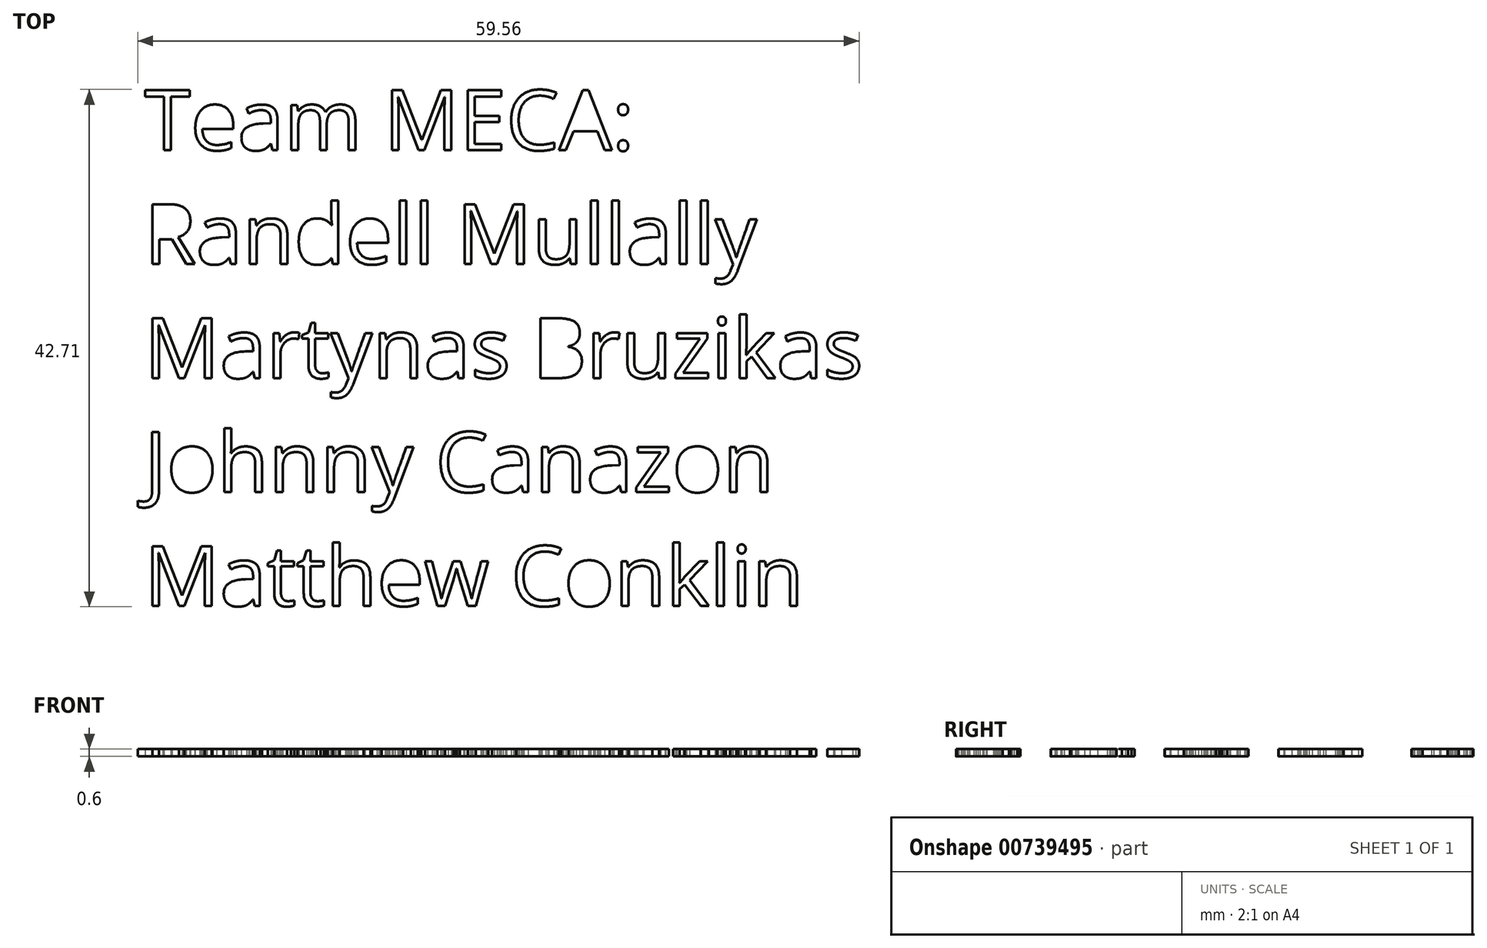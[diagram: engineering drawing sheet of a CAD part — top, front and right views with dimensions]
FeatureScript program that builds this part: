
annotation { "Feature Type Name" : "Feature", "Feature Type Description" : "" }
export const myFeature = defineFeature(function(context is Context, id is Id, definition is map)
    precondition{}
    {
        {
            var Q0;
            Q0=qCreatedBy(makeId("Top.planeOp"),FACE);
            var sketch = newSketch(context, id + "F0", { "sketchPlane" : qUnion([Q0])});
            skLineSegment(sketch, "E0.bottom", {"start": v(35, 50) * mm, "end": v(-35, 50) * mm});
            skLineSegment(sketch, "E0.top", {"start": v(35, -50) * mm, "end": v(-35, -50) * mm});
            skLineSegment(sketch, "E0.left", {"start": v(35, 50) * mm, "end": v(35, -50) * mm});
            skLineSegment(sketch, "E0.right", {"start": v(-35, 50) * mm, "end": v(-35, -50) * mm});
            skPoint(sketch, "E0.middle", {"position": v(0, 0) * mm});
            skText(sketch, "E1", { "text": "Team MECA:\nRandell Mullally\nMartynas Bruzikas\nJohnny Canazon\nMatthew Conklin", "fontName": "OpenSans-Regular.ttf"});
            const initialGuessF0  = {"E1": [-0.03, 0.03653, 1, 0, 0.00498]};
            skSetInitialGuess(sketch, initialGuessF0);
            skSolve(sketch);
        }
        {
            var Q0;
            Q0=makeQuery(id+"F0.imprint","IMPRINT",FACE,{"disambiguationData":[TD([[makeQuery(id+"F0.imprint","IMPRINT",EDGE,{"derivedFrom":sQuery(id+"F0.wireOp",EDGE,"E1.sketch_text.stroke-231")}),1.0]])]});
            var Q1;
            Q1=makeQuery(id+"F0.imprint","IMPRINT",FACE,{"disambiguationData":[TD([[makeQuery(id+"F0.imprint","IMPRINT",EDGE,{"derivedFrom":sQuery(id+"F0.wireOp",EDGE,"E1.sketch_text.stroke-254")}),1.0]])]});
            var Q2;
            Q2=makeQuery(id+"F0.imprint","IMPRINT",FACE,{"disambiguationData":[TD([[makeQuery(id+"F0.imprint","IMPRINT",EDGE,{"derivedFrom":sQuery(id+"F0.wireOp",EDGE,"E1.sketch_text.stroke-22")}),1.0]])]});
            var Q3;
            Q3=makeQuery(id+"F0.imprint","IMPRINT",FACE,{"disambiguationData":[TD([[makeQuery(id+"F0.imprint","IMPRINT",EDGE,{"derivedFrom":sQuery(id+"F0.wireOp",EDGE,"E1.sketch_text.stroke-46")}),1.0]])]});
            var Q4;
            Q4=makeQuery(id+"F0.imprint","IMPRINT",FACE,{"disambiguationData":[TD([[makeQuery(id+"F0.imprint","IMPRINT",EDGE,{"derivedFrom":sQuery(id+"F0.wireOp",EDGE,"E1.sketch_text.stroke-82")}),-1.0]])]});
            var Q5;
            Q5=makeQuery(id+"F0.imprint","IMPRINT",FACE,{"disambiguationData":[TD([[makeQuery(id+"F0.imprint","IMPRINT",EDGE,{"derivedFrom":sQuery(id+"F0.wireOp",EDGE,"E1.sketch_text.stroke-112")}),-1.0]])]});
            var Q6;
            Q6=makeQuery(id+"F0.imprint","IMPRINT",FACE,{"disambiguationData":[TD([[makeQuery(id+"F0.imprint","IMPRINT",EDGE,{"derivedFrom":sQuery(id+"F0.wireOp",EDGE,"E1.sketch_text.stroke-135")}),1.0]])]});
            var Q7;
            Q7=makeQuery(id+"F0.imprint","IMPRINT",FACE,{"disambiguationData":[TD([[makeQuery(id+"F0.imprint","IMPRINT",EDGE,{"derivedFrom":sQuery(id+"F0.wireOp",EDGE,"E1.sketch_text.stroke-165")}),1.0]])]});
            var Q8;
            Q8=makeQuery(id+"F0.imprint","IMPRINT",FACE,{"disambiguationData":[TD([[makeQuery(id+"F0.imprint","IMPRINT",EDGE,{"derivedFrom":sQuery(id+"F0.wireOp",EDGE,"E1.sketch_text.stroke-191")}),1.0]])]});
            var Q9;
            Q9=makeQuery(id+"F0.imprint","IMPRINT",FACE,{"disambiguationData":[TD([[makeQuery(id+"F0.imprint","IMPRINT",EDGE,{"derivedFrom":sQuery(id+"F0.wireOp",EDGE,"E1.sketch_text.stroke-1059")}),1.0]])]});
            var Q10;
            Q10=makeQuery(id+"F0.imprint","IMPRINT",FACE,{"disambiguationData":[TD([[makeQuery(id+"F0.imprint","IMPRINT",EDGE,{"derivedFrom":sQuery(id+"F0.wireOp",EDGE,"E1.sketch_text.stroke-746")}),-1.0]])]});
            var Q11;
            Q11=makeQuery(id+"F0.imprint","IMPRINT",FACE,{"disambiguationData":[TD([[makeQuery(id+"F0.imprint","IMPRINT",EDGE,{"derivedFrom":sQuery(id+"F0.wireOp",EDGE,"E1.sketch_text.stroke-615")}),-1.0]])]});
            var Q12;
            Q12=makeQuery(id+"F0.imprint","IMPRINT",FACE,{"disambiguationData":[TD([[makeQuery(id+"F0.imprint","IMPRINT",EDGE,{"derivedFrom":sQuery(id+"F0.wireOp",EDGE,"E1.sketch_text.stroke-534")}),1.0]])]});
            var Q13;
            Q13=makeQuery(id+"F0.imprint","IMPRINT",FACE,{"disambiguationData":[TD([[makeQuery(id+"F0.imprint","IMPRINT",EDGE,{"derivedFrom":sQuery(id+"F0.wireOp",EDGE,"E1.sketch_text.stroke-541")}),1.0]])]});
            var Q14;
            Q14=makeQuery(id+"F0.imprint","IMPRINT",FACE,{"disambiguationData":[TD([[makeQuery(id+"F0.imprint","IMPRINT",EDGE,{"derivedFrom":sQuery(id+"F0.wireOp",EDGE,"E1.sketch_text.stroke-329")}),1.0]])]});
            var Q15;
            Q15=makeQuery(id+"F0.imprint","IMPRINT",FACE,{"disambiguationData":[TD([[makeQuery(id+"F0.imprint","IMPRINT",EDGE,{"derivedFrom":sQuery(id+"F0.wireOp",EDGE,"E1.sketch_text.stroke-867")}),1.0]])]});
            var Q16;
            Q16=makeQuery(id+"F0.imprint","IMPRINT",FACE,{"disambiguationData":[TD([[makeQuery(id+"F0.imprint","IMPRINT",EDGE,{"derivedFrom":sQuery(id+"F0.wireOp",EDGE,"E1.sketch_text.stroke-8")}),-1.0]])]});
            var Q17;
            Q17=makeQuery(id+"F0.imprint","IMPRINT",FACE,{"disambiguationData":[TD([[makeQuery(id+"F0.imprint","IMPRINT",EDGE,{"derivedFrom":sQuery(id+"F0.wireOp",EDGE,"E1.sketch_text.stroke-398")}),1.0]])]});
            var Q18;
            Q18=makeQuery(id+"F0.imprint","IMPRINT",FACE,{"disambiguationData":[TD([[makeQuery(id+"F0.imprint","IMPRINT",EDGE,{"derivedFrom":sQuery(id+"F0.wireOp",EDGE,"E1.sketch_text.stroke-686")}),1.0]])]});
            var Q19;
            Q19=makeQuery(id+"F0.imprint","IMPRINT",FACE,{"disambiguationData":[TD([[makeQuery(id+"F0.imprint","IMPRINT",EDGE,{"derivedFrom":sQuery(id+"F0.wireOp",EDGE,"E1.sketch_text.stroke-0")}),-1.0]])]});
            var Q20;
            Q20=makeQuery(id+"F0.imprint","IMPRINT",FACE,{"disambiguationData":[TD([[makeQuery(id+"F0.imprint","IMPRINT",EDGE,{"derivedFrom":sQuery(id+"F0.wireOp",EDGE,"E1.sketch_text.stroke-54")}),-1.0]])]});
            var Q21;
            Q21=makeQuery(id+"F0.imprint","IMPRINT",FACE,{"disambiguationData":[TD([[makeQuery(id+"F0.imprint","IMPRINT",EDGE,{"derivedFrom":sQuery(id+"F0.wireOp",EDGE,"E1.sketch_text.stroke-100")}),-1.0]])]});
            var Q22;
            Q22=makeQuery(id+"F0.imprint","IMPRINT",FACE,{"disambiguationData":[TD([[makeQuery(id+"F0.imprint","IMPRINT",EDGE,{"derivedFrom":sQuery(id+"F0.wireOp",EDGE,"E1.sketch_text.stroke-140")}),-1.0]])]});
            var Q23;
            Q23=makeQuery(id+"F0.imprint","IMPRINT",FACE,{"disambiguationData":[TD([[makeQuery(id+"F0.imprint","IMPRINT",EDGE,{"derivedFrom":sQuery(id+"F0.wireOp",EDGE,"E1.sketch_text.stroke-148")}),-1.0]])]});
            var Q24;
            Q24=makeQuery(id+"F0.imprint","IMPRINT",FACE,{"disambiguationData":[TD([[makeQuery(id+"F0.imprint","IMPRINT",EDGE,{"derivedFrom":sQuery(id+"F0.wireOp",EDGE,"E1.sketch_text.stroke-199")}),-1.0]])]});
            var Q25;
            Q25=makeQuery(id+"F0.imprint","IMPRINT",FACE,{"disambiguationData":[TD([[makeQuery(id+"F0.imprint","IMPRINT",EDGE,{"derivedFrom":sQuery(id+"F0.wireOp",EDGE,"E1.sketch_text.stroke-490")}),1.0]])]});
            var Q26;
            Q26=makeQuery(id+"F0.imprint","IMPRINT",FACE,{"disambiguationData":[TD([[makeQuery(id+"F0.imprint","IMPRINT",EDGE,{"derivedFrom":sQuery(id+"F0.wireOp",EDGE,"E1.sketch_text.stroke-379")}),-1.0]])]});
            var Q27;
            Q27=makeQuery(id+"F0.imprint","IMPRINT",FACE,{"disambiguationData":[TD([[makeQuery(id+"F0.imprint","IMPRINT",EDGE,{"derivedFrom":sQuery(id+"F0.wireOp",EDGE,"E1.sketch_text.stroke-1035")}),-1.0]])]});
            var Q28;
            Q28=makeQuery(id+"F0.imprint","IMPRINT",FACE,{"disambiguationData":[TD([[makeQuery(id+"F0.imprint","IMPRINT",EDGE,{"derivedFrom":sQuery(id+"F0.wireOp",EDGE,"E1.sketch_text.stroke-729")}),-1.0]])]});
            var Q29;
            Q29=makeQuery(id+"F0.imprint","IMPRINT",FACE,{"disambiguationData":[TD([[makeQuery(id+"F0.imprint","IMPRINT",EDGE,{"derivedFrom":sQuery(id+"F0.wireOp",EDGE,"E1.sketch_text.stroke-240")}),-1.0]])]});
            var Q30;
            Q30=makeQuery(id+"F0.imprint","IMPRINT",FACE,{"disambiguationData":[TD([[makeQuery(id+"F0.imprint","IMPRINT",EDGE,{"derivedFrom":sQuery(id+"F0.wireOp",EDGE,"E1.sketch_text.stroke-1007")}),1.0]])]});
            var Q31;
            Q31=makeQuery(id+"F0.imprint","IMPRINT",FACE,{"disambiguationData":[TD([[makeQuery(id+"F0.imprint","IMPRINT",EDGE,{"derivedFrom":sQuery(id+"F0.wireOp",EDGE,"E1.sketch_text.stroke-694")}),-1.0]])]});
            var Q32;
            Q32=makeQuery(id+"F0.imprint","IMPRINT",FACE,{"disambiguationData":[TD([[makeQuery(id+"F0.imprint","IMPRINT",EDGE,{"derivedFrom":sQuery(id+"F0.wireOp",EDGE,"E1.sketch_text.stroke-438")}),-1.0]])]});
            var Q33;
            Q33=makeQuery(id+"F0.imprint","IMPRINT",FACE,{"disambiguationData":[TD([[makeQuery(id+"F0.imprint","IMPRINT",EDGE,{"derivedFrom":sQuery(id+"F0.wireOp",EDGE,"E1.sketch_text.stroke-310")}),-1.0]])]});
            var Q34;
            Q34=makeQuery(id+"F0.imprint","IMPRINT",FACE,{"disambiguationData":[TD([[makeQuery(id+"F0.imprint","IMPRINT",EDGE,{"derivedFrom":sQuery(id+"F0.wireOp",EDGE,"E1.sketch_text.stroke-1012")}),-1.0]])]});
            var Q35;
            Q35=makeQuery(id+"F0.imprint","IMPRINT",FACE,{"disambiguationData":[TD([[makeQuery(id+"F0.imprint","IMPRINT",EDGE,{"derivedFrom":sQuery(id+"F0.wireOp",EDGE,"E1.sketch_text.stroke-712")}),-1.0]])]});
            var Q36;
            Q36=makeQuery(id+"F0.imprint","IMPRINT",FACE,{"disambiguationData":[TD([[makeQuery(id+"F0.imprint","IMPRINT",EDGE,{"derivedFrom":sQuery(id+"F0.wireOp",EDGE,"E1.sketch_text.stroke-454")}),-1.0]])]});
            var Q37;
            Q37=makeQuery(id+"F0.imprint","IMPRINT",FACE,{"disambiguationData":[TD([[makeQuery(id+"F0.imprint","IMPRINT",EDGE,{"derivedFrom":sQuery(id+"F0.wireOp",EDGE,"E1.sketch_text.stroke-263")}),-1.0]])]});
            var Q38;
            Q38=makeQuery(id+"F0.imprint","IMPRINT",FACE,{"disambiguationData":[TD([[makeQuery(id+"F0.imprint","IMPRINT",EDGE,{"derivedFrom":sQuery(id+"F0.wireOp",EDGE,"E1.sketch_text.stroke-471")}),-1.0]])]});
            var Q39;
            Q39=makeQuery(id+"F0.imprint","IMPRINT",FACE,{"disambiguationData":[TD([[makeQuery(id+"F0.imprint","IMPRINT",EDGE,{"derivedFrom":sQuery(id+"F0.wireOp",EDGE,"E1.sketch_text.stroke-498")}),-1.0]])]});
            var Q40;
            Q40=makeQuery(id+"F0.imprint","IMPRINT",FACE,{"disambiguationData":[TD([[makeQuery(id+"F0.imprint","IMPRINT",EDGE,{"derivedFrom":sQuery(id+"F0.wireOp",EDGE,"E1.sketch_text.stroke-267")}),-1.0]])]});
            var Q41;
            Q41=makeQuery(id+"F0.imprint","IMPRINT",FACE,{"disambiguationData":[TD([[makeQuery(id+"F0.imprint","IMPRINT",EDGE,{"derivedFrom":sQuery(id+"F0.wireOp",EDGE,"E1.sketch_text.stroke-1067")}),-1.0]])]});
            var Q42;
            Q42=makeQuery(id+"F0.imprint","IMPRINT",FACE,{"disambiguationData":[TD([[makeQuery(id+"F0.imprint","IMPRINT",EDGE,{"derivedFrom":sQuery(id+"F0.wireOp",EDGE,"E1.sketch_text.stroke-762")}),-1.0]])]});
            var Q43;
            Q43=makeQuery(id+"F0.imprint","IMPRINT",FACE,{"disambiguationData":[TD([[makeQuery(id+"F0.imprint","IMPRINT",EDGE,{"derivedFrom":sQuery(id+"F0.wireOp",EDGE,"E1.sketch_text.stroke-285")}),-1.0]])]});
            var Q44;
            Q44=makeQuery(id+"F0.imprint","IMPRINT",FACE,{"disambiguationData":[TD([[makeQuery(id+"F0.imprint","IMPRINT",EDGE,{"derivedFrom":sQuery(id+"F0.wireOp",EDGE,"E1.sketch_text.stroke-677")}),-1.0]])]});
            var Q45;
            Q45=makeQuery(id+"F0.imprint","IMPRINT",FACE,{"disambiguationData":[TD([[makeQuery(id+"F0.imprint","IMPRINT",EDGE,{"derivedFrom":sQuery(id+"F0.wireOp",EDGE,"E1.sketch_text.stroke-1084")}),-1.0]])]});
            var Q46;
            Q46=makeQuery(id+"F0.imprint","IMPRINT",FACE,{"disambiguationData":[TD([[makeQuery(id+"F0.imprint","IMPRINT",EDGE,{"derivedFrom":sQuery(id+"F0.wireOp",EDGE,"E1.sketch_text.stroke-796")}),1.0]])]});
            var Q47;
            Q47=makeQuery(id+"F0.imprint","IMPRINT",FACE,{"disambiguationData":[TD([[makeQuery(id+"F0.imprint","IMPRINT",EDGE,{"derivedFrom":sQuery(id+"F0.wireOp",EDGE,"E1.sketch_text.stroke-302")}),-1.0]])]});
            var Q48;
            Q48=makeQuery(id+"F0.imprint","IMPRINT",FACE,{"disambiguationData":[TD([[makeQuery(id+"F0.imprint","IMPRINT",EDGE,{"derivedFrom":sQuery(id+"F0.wireOp",EDGE,"E1.sketch_text.stroke-777")}),-1.0]])]});
            var Q49;
            Q49=makeQuery(id+"F0.imprint","IMPRINT",FACE,{"disambiguationData":[TD([[makeQuery(id+"F0.imprint","IMPRINT",EDGE,{"derivedFrom":sQuery(id+"F0.wireOp",EDGE,"E1.sketch_text.stroke-1099")}),-1.0]])]});
            var Q50;
            Q50=makeQuery(id+"F0.imprint","IMPRINT",FACE,{"disambiguationData":[TD([[makeQuery(id+"F0.imprint","IMPRINT",EDGE,{"derivedFrom":sQuery(id+"F0.wireOp",EDGE,"E1.sketch_text.stroke-804")}),-1.0]])]});
            var Q51;
            Q51=makeQuery(id+"F0.imprint","IMPRINT",FACE,{"disambiguationData":[TD([[makeQuery(id+"F0.imprint","IMPRINT",EDGE,{"derivedFrom":sQuery(id+"F0.wireOp",EDGE,"E1.sketch_text.stroke-548")}),-1.0]])]});
            var Q52;
            Q52=makeQuery(id+"F0.imprint","IMPRINT",FACE,{"disambiguationData":[TD([[makeQuery(id+"F0.imprint","IMPRINT",EDGE,{"derivedFrom":sQuery(id+"F0.wireOp",EDGE,"E1.sketch_text.stroke-306")}),-1.0]])]});
            var Q53;
            Q53=makeQuery(id+"F0.imprint","IMPRINT",FACE,{"disambiguationData":[TD([[makeQuery(id+"F0.imprint","IMPRINT",EDGE,{"derivedFrom":sQuery(id+"F0.wireOp",EDGE,"E1.sketch_text.stroke-821")}),-1.0]])]});
            var Q54;
            Q54=makeQuery(id+"F0.imprint","IMPRINT",FACE,{"disambiguationData":[TD([[makeQuery(id+"F0.imprint","IMPRINT",EDGE,{"derivedFrom":sQuery(id+"F0.wireOp",EDGE,"E1.sketch_text.stroke-1103")}),-1.0]])]});
            var Q55;
            Q55=makeQuery(id+"F0.imprint","IMPRINT",FACE,{"disambiguationData":[TD([[makeQuery(id+"F0.imprint","IMPRINT",EDGE,{"derivedFrom":sQuery(id+"F0.wireOp",EDGE,"E1.sketch_text.stroke-840")}),1.0]])]});
            var Q56;
            Q56=makeQuery(id+"F0.imprint","IMPRINT",FACE,{"disambiguationData":[TD([[makeQuery(id+"F0.imprint","IMPRINT",EDGE,{"derivedFrom":sQuery(id+"F0.wireOp",EDGE,"E1.sketch_text.stroke-561")}),-1.0]])]});
            var Q57;
            Q57=makeQuery(id+"F0.imprint","IMPRINT",FACE,{"disambiguationData":[TD([[makeQuery(id+"F0.imprint","IMPRINT",EDGE,{"derivedFrom":sQuery(id+"F0.wireOp",EDGE,"E1.sketch_text.stroke-858")}),-1.0]])]});
            var Q58;
            Q58=makeQuery(id+"F0.imprint","IMPRINT",FACE,{"disambiguationData":[TD([[makeQuery(id+"F0.imprint","IMPRINT",EDGE,{"derivedFrom":sQuery(id+"F0.wireOp",EDGE,"E1.sketch_text.stroke-848")}),-1.0]])]});
            var Q59;
            Q59=makeQuery(id+"F0.imprint","IMPRINT",FACE,{"disambiguationData":[TD([[makeQuery(id+"F0.imprint","IMPRINT",EDGE,{"derivedFrom":sQuery(id+"F0.wireOp",EDGE,"E1.sketch_text.stroke-578")}),-1.0]])]});
            var Q60;
            Q60=makeQuery(id+"F0.imprint","IMPRINT",FACE,{"disambiguationData":[TD([[makeQuery(id+"F0.imprint","IMPRINT",EDGE,{"derivedFrom":sQuery(id+"F0.wireOp",EDGE,"E1.sketch_text.stroke-910")}),-1.0]])]});
            var Q61;
            Q61=makeQuery(id+"F0.imprint","IMPRINT",FACE,{"disambiguationData":[TD([[makeQuery(id+"F0.imprint","IMPRINT",EDGE,{"derivedFrom":sQuery(id+"F0.wireOp",EDGE,"E1.sketch_text.stroke-1115")}),-1.0]])]});
            var Q62;
            Q62=makeQuery(id+"F0.imprint","IMPRINT",FACE,{"disambiguationData":[TD([[makeQuery(id+"F0.imprint","IMPRINT",EDGE,{"derivedFrom":sQuery(id+"F0.wireOp",EDGE,"E1.sketch_text.stroke-588")}),-1.0]])]});
            var Q63;
            Q63=makeQuery(id+"F0.imprint","IMPRINT",FACE,{"disambiguationData":[TD([[makeQuery(id+"F0.imprint","IMPRINT",EDGE,{"derivedFrom":sQuery(id+"F0.wireOp",EDGE,"E1.sketch_text.stroke-875")}),-1.0]])]});
            var Q64;
            Q64=makeQuery(id+"F0.imprint","IMPRINT",FACE,{"disambiguationData":[TD([[makeQuery(id+"F0.imprint","IMPRINT",EDGE,{"derivedFrom":sQuery(id+"F0.wireOp",EDGE,"E1.sketch_text.stroke-341")}),-1.0]])]});
            var Q65;
            Q65=makeQuery(id+"F0.imprint","IMPRINT",FACE,{"disambiguationData":[TD([[makeQuery(id+"F0.imprint","IMPRINT",EDGE,{"derivedFrom":sQuery(id+"F0.wireOp",EDGE,"E1.sketch_text.stroke-993")}),-1.0]])]});
            var Q66;
            Q66=makeQuery(id+"F0.imprint","IMPRINT",FACE,{"disambiguationData":[TD([[makeQuery(id+"F0.imprint","IMPRINT",EDGE,{"derivedFrom":sQuery(id+"F0.wireOp",EDGE,"E1.sketch_text.stroke-892")}),-1.0]])]});
            var Q67;
            Q67=makeQuery(id+"F0.imprint","IMPRINT",FACE,{"disambiguationData":[TD([[makeQuery(id+"F0.imprint","IMPRINT",EDGE,{"derivedFrom":sQuery(id+"F0.wireOp",EDGE,"E1.sketch_text.stroke-600")}),-1.0]])]});
            var Q68;
            Q68=makeQuery(id+"F0.imprint","IMPRINT",FACE,{"disambiguationData":[TD([[makeQuery(id+"F0.imprint","IMPRINT",EDGE,{"derivedFrom":sQuery(id+"F0.wireOp",EDGE,"E1.sketch_text.stroke-345")}),-1.0]])]});
            var Q69;
            Q69=makeQuery(id+"F0.imprint","IMPRINT",FACE,{"disambiguationData":[TD([[makeQuery(id+"F0.imprint","IMPRINT",EDGE,{"derivedFrom":sQuery(id+"F0.wireOp",EDGE,"E1.sketch_text.stroke-1050")}),-1.0]])]});
            var Q70;
            Q70=makeQuery(id+"F0.imprint","IMPRINT",FACE,{"disambiguationData":[TD([[makeQuery(id+"F0.imprint","IMPRINT",EDGE,{"derivedFrom":sQuery(id+"F0.wireOp",EDGE,"E1.sketch_text.stroke-27")}),-1.0]])]});
            var Q71;
            Q71=makeQuery(id+"F0.imprint","IMPRINT",FACE,{"disambiguationData":[TD([[makeQuery(id+"F0.imprint","IMPRINT",EDGE,{"derivedFrom":sQuery(id+"F0.wireOp",EDGE,"E1.sketch_text.stroke-634")}),1.0]])]});
            var Q72;
            Q72=makeQuery(id+"F0.imprint","IMPRINT",FACE,{"disambiguationData":[TD([[makeQuery(id+"F0.imprint","IMPRINT",EDGE,{"derivedFrom":sQuery(id+"F0.wireOp",EDGE,"E1.sketch_text.stroke-361")}),-1.0]])]});
            var Q73;
            Q73=makeQuery(id+"F0.imprint","IMPRINT",FACE,{"disambiguationData":[TD([[makeQuery(id+"F0.imprint","IMPRINT",EDGE,{"derivedFrom":sQuery(id+"F0.wireOp",EDGE,"E1.sketch_text.stroke-523")}),-1.0]])]});
            var Q74;
            Q74=makeQuery(id+"F0.imprint","IMPRINT",FACE,{"disambiguationData":[TD([[makeQuery(id+"F0.imprint","IMPRINT",EDGE,{"derivedFrom":sQuery(id+"F0.wireOp",EDGE,"E1.sketch_text.stroke-127")}),-1.0]])]});
            var Q75;
            Q75=makeQuery(id+"F0.imprint","IMPRINT",FACE,{"disambiguationData":[TD([[makeQuery(id+"F0.imprint","IMPRINT",EDGE,{"derivedFrom":sQuery(id+"F0.wireOp",EDGE,"E1.sketch_text.stroke-937")}),-1.0]])]});
            var Q76;
            Q76=makeQuery(id+"F0.imprint","IMPRINT",FACE,{"disambiguationData":[TD([[makeQuery(id+"F0.imprint","IMPRINT",EDGE,{"derivedFrom":sQuery(id+"F0.wireOp",EDGE,"E1.sketch_text.stroke-642")}),-1.0]])]});
            var Q77;
            Q77=makeQuery(id+"F0.imprint","IMPRINT",FACE,{"disambiguationData":[TD([[makeQuery(id+"F0.imprint","IMPRINT",EDGE,{"derivedFrom":sQuery(id+"F0.wireOp",EDGE,"E1.sketch_text.stroke-154")}),-1.0]])]});
            var Q78;
            Q78=makeQuery(id+"F0.imprint","IMPRINT",FACE,{"disambiguationData":[TD([[makeQuery(id+"F0.imprint","IMPRINT",EDGE,{"derivedFrom":sQuery(id+"F0.wireOp",EDGE,"E1.sketch_text.stroke-956")}),-1.0]])]});
            var Q79;
            Q79=makeQuery(id+"F0.imprint","IMPRINT",FACE,{"disambiguationData":[TD([[makeQuery(id+"F0.imprint","IMPRINT",EDGE,{"derivedFrom":sQuery(id+"F0.wireOp",EDGE,"E1.sketch_text.stroke-667")}),-1.0]])]});
            var Q80;
            Q80=makeQuery(id+"F0.imprint","IMPRINT",FACE,{"disambiguationData":[TD([[makeQuery(id+"F0.imprint","IMPRINT",EDGE,{"derivedFrom":sQuery(id+"F0.wireOp",EDGE,"E1.sketch_text.stroke-406")}),-1.0]])]});
            var Q81;
            Q81=makeQuery(id+"F0.imprint","IMPRINT",FACE,{"disambiguationData":[TD([[makeQuery(id+"F0.imprint","IMPRINT",EDGE,{"derivedFrom":sQuery(id+"F0.wireOp",EDGE,"E1.sketch_text.stroke-172")}),-1.0]])]});
            var Q82;
            Q82=makeQuery(id+"F0.imprint","IMPRINT",FACE,{"disambiguationData":[TD([[makeQuery(id+"F0.imprint","IMPRINT",EDGE,{"derivedFrom":sQuery(id+"F0.wireOp",EDGE,"E1.sketch_text.stroke-975")}),-1.0]])]});
            var Q83;
            Q83=makeQuery(id+"F0.imprint","IMPRINT",FACE,{"disambiguationData":[TD([[makeQuery(id+"F0.imprint","IMPRINT",EDGE,{"derivedFrom":sQuery(id+"F0.wireOp",EDGE,"E1.sketch_text.stroke-419")}),-1.0]])]});
            var Q84;
            Q84=makeQuery(id+"F0.imprint","IMPRINT",FACE,{"disambiguationData":[TD([[makeQuery(id+"F0.imprint","IMPRINT",EDGE,{"derivedFrom":sQuery(id+"F0.wireOp",EDGE,"E1.sketch_text.stroke-216")}),-1.0]])]});
            var Q85;
            Q85=makeQuery(id+"F0.imprint","IMPRINT",FACE,{"disambiguationData":[TD([[makeQuery(id+"F0.imprint","IMPRINT",EDGE,{"derivedFrom":sQuery(id+"F0.wireOp",EDGE,"E1.sketch_text.stroke-259")}),-1.0]])]});
            var Q86;
            Q86=makeQuery(id+"F0.imprint","IMPRINT",FACE,{"disambiguationData":[TD([[makeQuery(id+"F0.imprint","IMPRINT",EDGE,{"derivedFrom":sQuery(id+"F0.wireOp",EDGE,"E1.sketch_text.stroke-1107")}),-1.0]])]});
            var Q87;
            Q87=makeQuery(id+"F0.imprint","IMPRINT",FACE,{"disambiguationData":[TD([[makeQuery(id+"F0.imprint","IMPRINT",EDGE,{"derivedFrom":sQuery(id+"F0.wireOp",EDGE,"E1.sketch_text.stroke-337")}),-1.0]])]});
            var Q88;
            Q88=makeQuery(id+"F0.imprint","IMPRINT",FACE,{"disambiguationData":[TD([[makeQuery(id+"F0.imprint","IMPRINT",EDGE,{"derivedFrom":sQuery(id+"F0.wireOp",EDGE,"E1.sketch_text.stroke-592")}),-1.0]])]});
            var Q89;
            Q89=makeQuery(id+"F0.imprint","IMPRINT",FACE,{"disambiguationData":[TD([[makeQuery(id+"F0.imprint","IMPRINT",EDGE,{"derivedFrom":sQuery(id+"F0.wireOp",EDGE,"E1.sketch_text.stroke-929")}),1.0]])]});
            extrude(context, id + "F1", {"entities" : qUnion([Q0, Q1, Q2, Q3, Q4, Q5, Q6, Q7, Q8, Q9, Q10, Q11, Q12, Q13, Q14, Q15, Q16, Q17, Q18, Q19, Q20, Q21, Q22, Q23, Q24, Q25, Q26, Q27, Q28, Q29, Q30, Q31, Q32, Q33, Q34, Q35, Q36, Q37, Q38, Q39, Q40, Q41, Q42, Q43, Q44, Q45, Q46, Q47, Q48, Q49, Q50, Q51, Q52, Q53, Q54, Q55, Q56, Q57, Q58, Q59, Q60, Q61, Q62, Q63, Q64, Q65, Q66, Q67, Q68, Q69, Q70, Q71, Q72, Q73, Q74, Q75, Q76, Q77, Q78, Q79, Q80, Q81, Q82, Q83, Q84, Q85, Q86, Q87, Q88, Q89]), "depth" : .6 * mm, "offsetDistance" : 25.4 * mm});
        }
    });
